# Revit family: TMI - D8900 - Base_1 Kneespace Drawer1
name_source: partatom
category: Casework
revit_build: Autodesk Revit 2016 (Build: 20150220_1215(x64)
units: mm (PartAtom-declared; Revit-internal decimal feet)

## family parameters
Always vertical = Yes
Cut with Voids When Loaded = No
OmniClass Number = 23.40.35.14.11
OmniClass Title = Modular Casework
Room Calculation Point = No
Shared = No
Work Plane-Based = No

## types (6) — shared parameters
Cabinet Finish = Plastic Laminate
Casework Back Thickness = 3/4"
Casework Thickness = 3/4"
Countertop Height = 30"
Countertop Thickness = 1 1/4"
Depth = 24"
Description = Base, 1 Kneespace Drawer
Distance of Door from Top of Casework = 1/4"
Door Thickness = 3/4"
Drawer Height = 4"
Height = 28 3/4"
Manufacturer = TMI Systems Corporation
Model = D8900
URL = www.tmisystems.com

## per-type parameters (varying)
| type | Width |
| 30" x 4" x 24" | 30" |
| 27" x 4" x 24" | 27" |
| 24" x 4" x 24" | 24" |
| 21" x 4" x 24" | 21" |
| 18" x 4" x 24" | 18" |
| 15" x 4" x 24" | 15" |

## geometry (parser evidence)
native form markers: Blend x6, Sweep x5
no freeform markers — native parametric forms only
